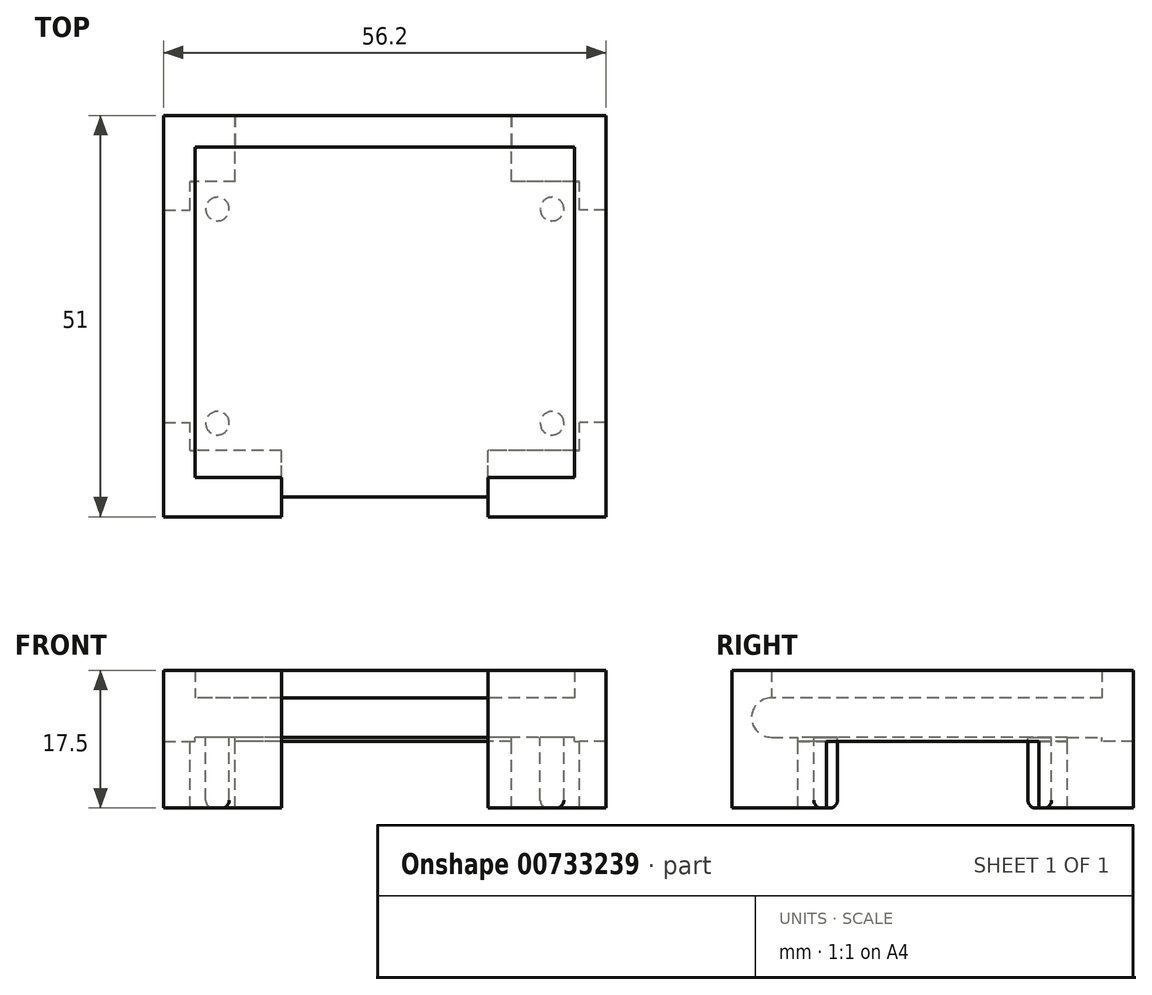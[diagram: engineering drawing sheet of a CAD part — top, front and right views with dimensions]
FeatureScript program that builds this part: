
annotation { "Feature Type Name" : "Feature", "Feature Type Description" : "" }
export const myFeature = defineFeature(function(context is Context, id is Id, definition is map)
    precondition{}
    {
        {
            var Q0;
            Q0=qCreatedBy(makeId("Top.planeOp"),FACE);
            var sketch = newSketch(context, id + "F0", { "sketchPlane" : qUnion([Q0])});
            skLineSegment(sketch, "E0.top", {"start": v(23.1, -20.5) * mm, "end": v(-23.1, -20.5) * mm});
            skPoint(sketch, "E0.middle", {"position": v(0, 0) * mm});
            skLineSegment(sketch, "E1.0", {"start": v(-28.1, 25.5) * mm, "end": v(-28.1, -25.5) * mm});
            skLineSegment(sketch, "E1.1", {"start": v(28.1, 25.5) * mm, "end": v(-28.1, 25.5) * mm});
            skLineSegment(sketch, "E1.2", {"start": v(28.1, 25.5) * mm, "end": v(28.1, -25.5) * mm});
            skLineSegment(sketch, "E1.3", {"start": v(28.1, -25.5) * mm, "end": v(-28.1, -25.5) * mm});
            skLineSegment(sketch, "E2.bottom", {"start": v(-28.1, -25.5) * mm, "end": v(-13.1, -25.5) * mm});
            skLineSegment(sketch, "E2.top", {"start": v(-28.1, -20.5) * mm, "end": v(-13.1, -20.5) * mm});
            skLineSegment(sketch, "E2.left", {"start": v(-28.1, -25.5) * mm, "end": v(-28.1, -20.5) * mm});
            skLineSegment(sketch, "E2.right", {"start": v(-13.1, -25.5) * mm, "end": v(-13.1, -20.5) * mm});
            skLineSegment(sketch, "E3.bottom", {"start": v(28.1, -25.5) * mm, "end": v(13.1, -25.5) * mm});
            skLineSegment(sketch, "E3.top", {"start": v(28.1, -20.5) * mm, "end": v(13.1, -20.5) * mm});
            skLineSegment(sketch, "E3.left", {"start": v(28.1, -25.5) * mm, "end": v(28.1, -20.5) * mm});
            skLineSegment(sketch, "E3.right", {"start": v(13.1, -25.5) * mm, "end": v(13.1, -20.5) * mm});
            skLineSegment(sketch, "E4.bottom", {"start": v(-13.1, -20.5) * mm, "end": v(13.1, -20.5) * mm});
            skLineSegment(sketch, "E4.top", {"start": v(-13.1, -23) * mm, "end": v(13.1, -23) * mm});
            skLineSegment(sketch, "E4.left", {"start": v(-13.1, -20.5) * mm, "end": v(-13.1, -23) * mm});
            skLineSegment(sketch, "E4.right", {"start": v(13.1, -20.5) * mm, "end": v(13.1, -23) * mm});
            skLineSegment(sketch, "E5.0", {"start": v(-24.1, 21.5) * mm, "end": v(-24.1, -20.5) * mm});
            skLineSegment(sketch, "E5.1", {"start": v(24.1, 21.5) * mm, "end": v(-24.1, 21.5) * mm});
            skLineSegment(sketch, "E5.2", {"start": v(24.1, 21.5) * mm, "end": v(24.1, -20.5) * mm});
            skPoint(sketch, "E0.left.start.orphan", {"position": v(23.1, 20.5) * mm});
            skPoint(sketch, "E0.right.start.orphan", {"position": v(-23.1, 20.5) * mm});
            skSolve(sketch);
        }
        {
            var Q0;
            {var subQ5=sQuery(id+"F0.wireOp",EDGE,"E4.top");Q0=makeQuery(id+"F0.imprint","IMPRINT",FACE,{"disambiguationData":[TD([[makeQuery(id+"F0.imprint","IMPRINT",EDGE,{"derivedFrom":subQ5}),1.0]])]});}
            var Q1;
            {var subQ3=sQuery(id+"F0.wireOp",EDGE,"E5.0");Q1=makeQuery(id+"F0.imprint","IMPRINT",FACE,{"disambiguationData":[TD([[makeQuery(id+"F0.imprint","IMPRINT",EDGE,{"derivedFrom":subQ3}),1.0]])]});}
            extrude(context, id + "F1", {"entities" : qUnion([Q0, Q1]), "depth" : 5 * mm, "offsetDistance" : 25 * mm});
        }
        {
            var Q0;
            {var subQ5=sQuery(id+"F0.wireOp",EDGE,"E2.top");var subQ8=sQuery(id+"F0.wireOp",EDGE,"E0.top");var subQ9=makeQuery(id+"F0.imprint","INTERSECT",VERTEX,{"derivedFrom":[subQ8,subQ5]});Q0=makeQuery(id+"F0.imprint","IMPRINT",FACE,{"disambiguationData":[TD([[makeQuery(id+"F0.imprint","IMPRINT",EDGE,{"disambiguationData":[TD([[subQ9,1.0]])],"derivedFrom":subQ8}),1.0]])]});}
            var Q1;
            {var subQ6=sQuery(id+"F0.wireOp",EDGE,"E1.1");Q1=makeQuery(id+"F0.imprint","IMPRINT",FACE,{"disambiguationData":[TD([[makeQuery(id+"F0.imprint","IMPRINT",EDGE,{"derivedFrom":subQ6}),1.0]])]});}
            var Q2;
            {var subQ6=sQuery(id+"F0.wireOp",EDGE,"E3.right");var subQ9=sQuery(id+"F0.wireOp",EDGE,"E0.top");var subQ10=makeQuery(id+"F0.imprint","INTERSECT",VERTEX,{"derivedFrom":[subQ9,subQ6]});Q2=makeQuery(id+"F0.imprint","IMPRINT",FACE,{"disambiguationData":[TD([[makeQuery(id+"F0.imprint","IMPRINT",EDGE,{"disambiguationData":[TD([[subQ10,1.0]])],"derivedFrom":subQ9}),1.0]])]});}
            extrude(context, id + "F2", {"entities" : qUnion([Q0, Q1, Q2]), "operationType" : NewBodyOperationType.ADD, "depth" : 8.5 * mm, "offsetDistance" : 25 * mm});
        }
        {
            var Q0;
            {var subQ0=sQuery(id+"F0.wireOp",EDGE,"E5.2");var subQ1=sQuery(id+"F0.wireOp",EDGE,"E5.1");var subQ2=sQuery(id+"F0.wireOp",EDGE,"E5.0");var subQ3=sQuery(id+"F0.wireOp",EDGE,"E3.right");var subQ4=sQuery(id+"F0.wireOp",EDGE,"E3.top");var subQ5=sQuery(id+"F0.wireOp",EDGE,"E2.right");var subQ6=sQuery(id+"F0.wireOp",EDGE,"E2.top");var subQ7=sQuery(id+"F0.wireOp",EDGE,"E0.top");Q0=makeQuery(id+"F2.boolean.opBoolean","MERGE",FACE,{"derivedFrom":[makeQuery(id+"F1.opExtrude","CAP_FACE",FACE,{"disambiguationData":[OSD([subQ7,subQ6,subQ5,subQ4,subQ3,sQuery(id+"F0.wireOp",EDGE,"E4.top"),subQ2,subQ1,subQ0])],"isStart":true}),makeQuery(id+"F2.opExtrude","CAP_FACE",FACE,{"disambiguationData":[OSD([subQ7,sQuery(id+"F0.wireOp",EDGE,"E1.0"),sQuery(id+"F0.wireOp",EDGE,"E1.1"),sQuery(id+"F0.wireOp",EDGE,"E1.2"),sQuery(id+"F0.wireOp",EDGE,"E1.3"),subQ6,subQ5,subQ4,subQ3,subQ2,subQ1,subQ0])],"isStart":true})]});}
            var sketch = newSketch(context, id + "F3", { "sketchPlane" : qUnion([Q0])});
            skLineSegment(sketch, "E6.bottom", {"start": v(23.75, -16.1) * mm, "end": v(-23.75, -16.1) * mm});
            skLineSegment(sketch, "E6.top", {"start": v(23.75, 16.1) * mm, "end": v(-23.75, 16.1) * mm});
            skLineSegment(sketch, "E6.left", {"start": v(23.75, -16.1) * mm, "end": v(23.75, 16.1) * mm});
            skLineSegment(sketch, "E6.right", {"start": v(-23.75, -16.1) * mm, "end": v(-23.75, 16.1) * mm});
            skPoint(sketch, "E6.middle", {"position": v(0, 0) * mm});
            skLineSegment(sketch, "E7.0", {"start": v(24.75, -17.1) * mm, "end": v(-24.75, -17.1) * mm});
            skLineSegment(sketch, "E7.1", {"start": v(24.75, -17.1) * mm, "end": v(24.75, 17.1) * mm});
            skLineSegment(sketch, "E7.2", {"start": v(24.75, 17.1) * mm, "end": v(-24.75, 17.1) * mm});
            skLineSegment(sketch, "E7.3", {"start": v(-24.75, -17.1) * mm, "end": v(-24.75, 17.1) * mm});
            skCircle(sketch, "E8", {"center": v(-21.25, 13.6) * mm, "radius": 1.5 * mm});
            skCircle(sketch, "E9", {"center": v(-21.25, -13.6) * mm, "radius": 1.5 * mm});
            skCircle(sketch, "E10", {"center": v(21.25, -13.6) * mm, "radius": 1.5 * mm});
            skCircle(sketch, "E11", {"center": v(21.25, 13.6) * mm, "radius": 1.5 * mm});
            skLineSegment(sketch, "E12", {"start": v(-13.1, 25.5) * mm, "end": v(-13.1, 17.1) * mm});
            skLineSegment(sketch, "E13", {"start": v(13.1, 25.5) * mm, "end": v(13.1, 17.1) * mm});
            skLineSegment(sketch, "E14", {"start": v(24.75, 13.5) * mm, "end": v(28.1, 13.5) * mm});
            skLineSegment(sketch, "E15", {"start": v(24.75, -13.5) * mm, "end": v(28.1, -13.5) * mm});
            skLineSegment(sketch, "E16", {"start": v(16.1, -17.1) * mm, "end": v(16.1, -25.5) * mm});
            skLineSegment(sketch, "E17", {"start": v(-19, -17.1) * mm, "end": v(-19, -25.5) * mm});
            skLineSegment(sketch, "E18", {"start": v(-24.75, -13.5) * mm, "end": v(-28.1, -13.5) * mm});
            skLineSegment(sketch, "E19", {"start": v(-24.75, 13.5) * mm, "end": v(-28.1, 13.5) * mm});
            skSolve(sketch);
        }
        {
            var Q0;
            {var subQ7=sQuery(id+"F3.wireOp",EDGE,"E19");Q0=makeQuery(id+"F3.imprint","IMPRINT",FACE,{"disambiguationData":[TD([[makeQuery(id+"F3.imprint","IMPRINT",EDGE,{"derivedFrom":subQ7}),-1.0]])]});}
            var Q1;
            {var subQ0=sQuery(id+"F3.wireOp",EDGE,"E17");Q1=makeQuery(id+"F3.imprint","IMPRINT",FACE,{"disambiguationData":[TD([[makeQuery(id+"F3.imprint","IMPRINT",EDGE,{"derivedFrom":subQ0}),-1.0]])]});}
            var Q2;
            {var subQ7=sQuery(id+"F3.wireOp",EDGE,"E15");Q2=makeQuery(id+"F3.imprint","IMPRINT",FACE,{"disambiguationData":[TD([[makeQuery(id+"F3.imprint","IMPRINT",EDGE,{"derivedFrom":subQ7}),-1.0]])]});}
            var Q3;
            {var subQ7=sQuery(id+"F3.wireOp",EDGE,"E14");Q3=makeQuery(id+"F3.imprint","IMPRINT",FACE,{"disambiguationData":[TD([[makeQuery(id+"F3.imprint","IMPRINT",EDGE,{"derivedFrom":subQ7}),1.0]])]});}
            extrude(context, id + "F4", {"entities" : qUnion([Q0, Q1, Q2, Q3]), "operationType" : NewBodyOperationType.ADD, "depth" : 9 * mm, "offsetDistance" : 25 * mm});
        }
        {
            var Q0;
            Q0=makeQuery(id+"F3.imprint","IMPRINT",FACE,{"disambiguationData":[TD([[makeQuery(id+"F3.imprint","IMPRINT",EDGE,{"derivedFrom":sQuery(id+"F3.wireOp",EDGE,"E8")}),1.0]])]});
            var Q1;
            Q1=makeQuery(id+"F3.imprint","IMPRINT",FACE,{"disambiguationData":[TD([[makeQuery(id+"F3.imprint","IMPRINT",EDGE,{"derivedFrom":sQuery(id+"F3.wireOp",EDGE,"E9")}),1.0]])]});
            var Q2;
            Q2=makeQuery(id+"F3.imprint","IMPRINT",FACE,{"disambiguationData":[TD([[makeQuery(id+"F3.imprint","IMPRINT",EDGE,{"derivedFrom":sQuery(id+"F3.wireOp",EDGE,"E10")}),1.0]])]});
            var Q3;
            Q3=makeQuery(id+"F3.imprint","IMPRINT",FACE,{"disambiguationData":[TD([[makeQuery(id+"F3.imprint","IMPRINT",EDGE,{"derivedFrom":sQuery(id+"F3.wireOp",EDGE,"E11")}),1.0]])]});
            var Q4;
            Q4=makeQuery(id+"F2.opExtrude","CAP_FACE",FACE,{"disambiguationData":[OSD([sQuery(id+"F0.wireOp",EDGE,"E0.top"),sQuery(id+"F0.wireOp",EDGE,"E1.0"),sQuery(id+"F0.wireOp",EDGE,"E1.1"),sQuery(id+"F0.wireOp",EDGE,"E1.2"),sQuery(id+"F0.wireOp",EDGE,"E1.3"),sQuery(id+"F0.wireOp",EDGE,"E2.top"),sQuery(id+"F0.wireOp",EDGE,"E2.right"),sQuery(id+"F0.wireOp",EDGE,"E3.top"),sQuery(id+"F0.wireOp",EDGE,"E3.right"),sQuery(id+"F0.wireOp",EDGE,"E5.0"),sQuery(id+"F0.wireOp",EDGE,"E5.1"),sQuery(id+"F0.wireOp",EDGE,"E5.2")])],"isStart":false});
            extrude(context, id + "F5", {"entities" : qUnion([Q0, Q1, Q2, Q3, Q4]), "operationType" : NewBodyOperationType.ADD, "depth" : 9 * mm, "offsetDistance" : 25 * mm});
        }
        {
            var Q0;
            Q0=makeQuery(id+"F5.opExtrude","CAP_EDGE",EDGE,{"disambiguationData":[OSD([sQuery(id+"F3.wireOp",EDGE,"E9")])],"isStart":false});
            var Q1;
            Q1=makeQuery(id+"F5.opExtrude","CAP_EDGE",EDGE,{"disambiguationData":[OSD([sQuery(id+"F3.wireOp",EDGE,"E8")])],"isStart":false});
            var Q2;
            Q2=makeQuery(id+"F5.opExtrude","CAP_EDGE",EDGE,{"disambiguationData":[OSD([sQuery(id+"F3.wireOp",EDGE,"E11")])],"isStart":false});
            var Q3;
            Q3=makeQuery(id+"F5.opExtrude","CAP_EDGE",EDGE,{"disambiguationData":[OSD([sQuery(id+"F3.wireOp",EDGE,"E10")])],"isStart":false});
            fillet(context, id + "F6", {"entities" : qUnion([Q0, Q1, Q2, Q3]), "radius" : 1 * mm, "tangentPropagation" : true, "allowEdgeOverflow" : false});
        }
        {
            var Q0;
            Q0=makeQuery(id+"F1.opExtrude","CAP_EDGE",EDGE,{"disambiguationData":[OSD([sQuery(id+"F0.wireOp",EDGE,"E4.top")])],"isStart":true});
            var Q1;
            Q1=makeQuery(id+"F1.opExtrude","CAP_EDGE",EDGE,{"disambiguationData":[OSD([sQuery(id+"F0.wireOp",EDGE,"E4.top")])],"isStart":false});
            fillet(context, id + "F7", {"entities" : qUnion([Q0, Q1]), "radius" : 2.5 * mm, "tangentPropagation" : true, "allowEdgeOverflow" : false});
        }
    });
